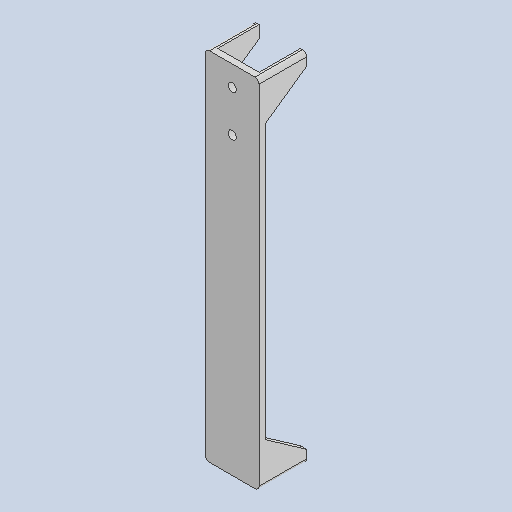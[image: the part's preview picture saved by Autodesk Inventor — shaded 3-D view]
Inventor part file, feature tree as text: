
AUTODESK INVENTOR PART (.ipt)
format: ipt  version: 2022 (Build 260153000, 153)  size: 127,488 bytes
history: native  units: mm
features: extrude x3, other x3, sketch x2, chamfer x2, reference x2, plane x1, mirror x1, fillet x1
ambient origin geometry x8: Origin, YZ Plane, XZ Plane, XY Plane, X Axis, Y Axis, Z Axis, Center Point
bodies: Solid1 (feature_tree)
feature tree (15):
  sketch  "Sketch1"  dims[d0=20.0mm d1=172.5mm]
  extrude  "Extrusion1"  Depth=172.5mm
  extrude  "Extrusion2"  Depth=3.0mm
  chamfer  "Chamfer1"  Distance=3.0mm
  chamfer  "Chamfer2"  Distance=20.0mm
  extrude  "Extrusion3"  Depth=20.0mm TaperAngle=0.0deg
  plane  "Work Plane2"
  mirror  "Mirror2"
  fillet  "Fillet1"  Radius=20.0mm
  sketch  "Sketch2"  dims[d2=3.0mm d3=3.0mm d4=3.0mm d5=0.0mm d6=20.0mm d7=20.0mm d8=0.0mm d9=20.0mm d10=2.0mm d11=6.108652mm d12=20.0mm d13=2.0mm d14=6.108652mm d15=2.0mm d16=0.0mm d17=0.0mm]
  reference  "Reference1"
  reference  "Reference2"
  parser-record x1  (decoder bookkeeping rows leaked as tree rows — omitted from the tree; the rows remain in map.json)
  other  "Bibble0.iam"
  other  "2040 Z Axis Upright:2"
note: 1 file-system path scrubbed to <path> (originals preserved in map.json)
